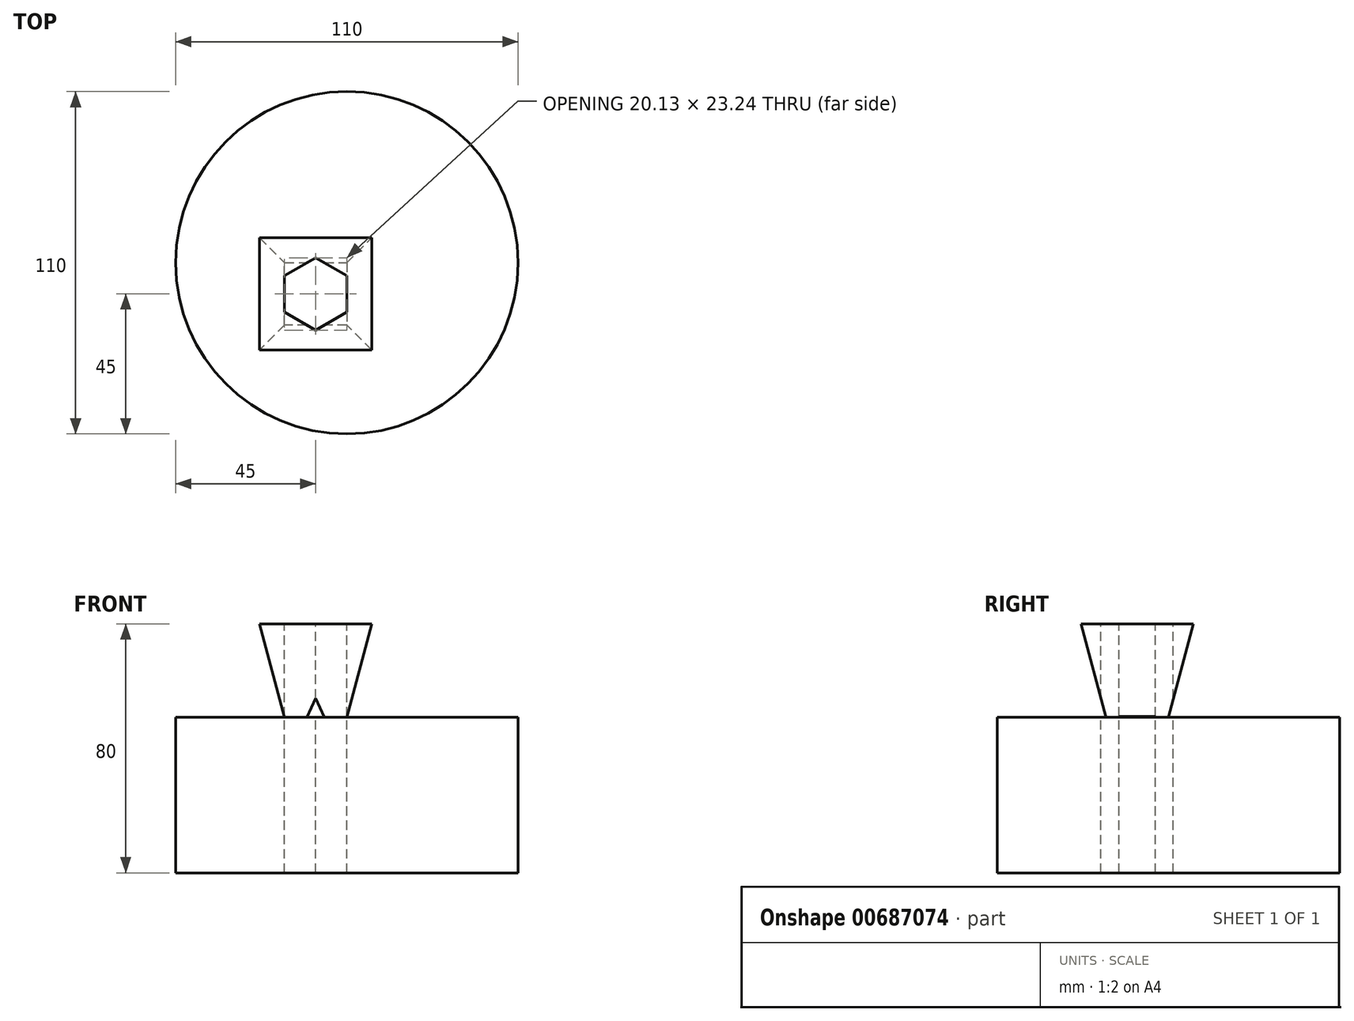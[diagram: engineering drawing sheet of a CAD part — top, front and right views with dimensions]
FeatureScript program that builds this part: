
annotation { "Feature Type Name" : "Feature", "Feature Type Description" : "" }
export const myFeature = defineFeature(function(context is Context, id is Id, definition is map)
    precondition{}
    {
        {
            var Q0;
            Q0=qCreatedBy(makeId("Top.planeOp"),FACE);
            var sketch = newSketch(context, id + "F0", { "sketchPlane" : qUnion([Q0])});
            skCircle(sketch, "E0", {"center": v(0, 0) * mm, "radius": 55 * mm});
            skSolve(sketch);
        }
        {
            var Q0;
            Q0 = qSketchRegion(id + "F0", true);
            extrude(context, id + "F1", {"entities" : qUnion([Q0]), "depth" : 50 * mm, "offsetDistance" : 25 * mm});
        }
        {
            var Q0;
            Q0=makeQuery(id+"F1.opExtrude","CAP_FACE",FACE,{"disambiguationData":[OSD([sQuery(id+"F0.wireOp",EDGE,"E0")])],"isStart":false});
            var sketch = newSketch(context, id + "F2", { "sketchPlane" : qUnion([Q0])});
            skLineSegment(sketch, "E1.bottom", {"start": v(0, 0) * mm, "end": v(-20, 0) * mm});
            skLineSegment(sketch, "E1.top", {"start": v(0, -20) * mm, "end": v(-20, -20) * mm});
            skLineSegment(sketch, "E1.left", {"start": v(0, 0) * mm, "end": v(0, -20) * mm});
            skLineSegment(sketch, "E1.right", {"start": v(-20, 0) * mm, "end": v(-20, -20) * mm});
            skSolve(sketch);
        }
        {
            var Q0;
            Q0 = qSketchRegion(id + "F2", true);
            extrude(context, id + "F3", {"entities" : qUnion([Q0]), "operationType" : NewBodyOperationType.ADD, "depth" : 30 * mm, "offsetDistance" : 25 * mm, "hasDraft" : true, "draftAngle" : 15 * degree});
        }
        {
            var Q0;
            Q0=makeQuery(id+"F3.opExtrude","CAP_FACE",FACE,{"disambiguationData":[OSD([sQuery(id+"F2.wireOp",EDGE,"E1.bottom"),sQuery(id+"F2.wireOp",EDGE,"E1.top"),sQuery(id+"F2.wireOp",EDGE,"E1.left"),sQuery(id+"F2.wireOp",EDGE,"E1.right")])],"isStart":false});
            var sketch = newSketch(context, id + "F4", { "sketchPlane" : qUnion([Q0])});
            skCircle(sketch, "E2.cCircle", {"center": v(-10, -10) * mm, "radius": 10.06 * mm, "construction": true});
            skLineSegment(sketch, "E2.0", {"start": v(-10, 1.62) * mm, "end": v(0.06, -4.19) * mm});
            skLineSegment(sketch, "E2.1", {"start": v(0.06, -4.19) * mm, "end": v(0.06, -15.81) * mm});
            skLineSegment(sketch, "E2.2", {"start": v(0.06, -15.81) * mm, "end": v(-10, -21.62) * mm});
            skLineSegment(sketch, "E2.3", {"start": v(-10, -21.62) * mm, "end": v(-20.06, -15.81) * mm});
            skLineSegment(sketch, "E2.4", {"start": v(-20.06, -15.81) * mm, "end": v(-20.06, -4.19) * mm});
            skLineSegment(sketch, "E2.5", {"start": v(-20.06, -4.19) * mm, "end": v(-10, 1.62) * mm});
            skPoint(sketch, "E2.0.midPoint", {"position": v(-4.97, -1.28) * mm});
            skLineSegment(sketch, "E3", {"start": v(-28.04, 8.04) * mm, "end": v(8.04, -28.04) * mm, "construction": true});
            skSolve(sketch);
        }
        {
            var Q0;
            Q0 = qSketchRegion(id + "F4", true);
            extrude(context, id + "F5", {"entities" : qUnion([Q0]), "operationType" : NewBodyOperationType.REMOVE, "oppositeDirection" : true, "depth" : 100 * mm, "offsetDistance" : 25 * mm});
        }
    });
